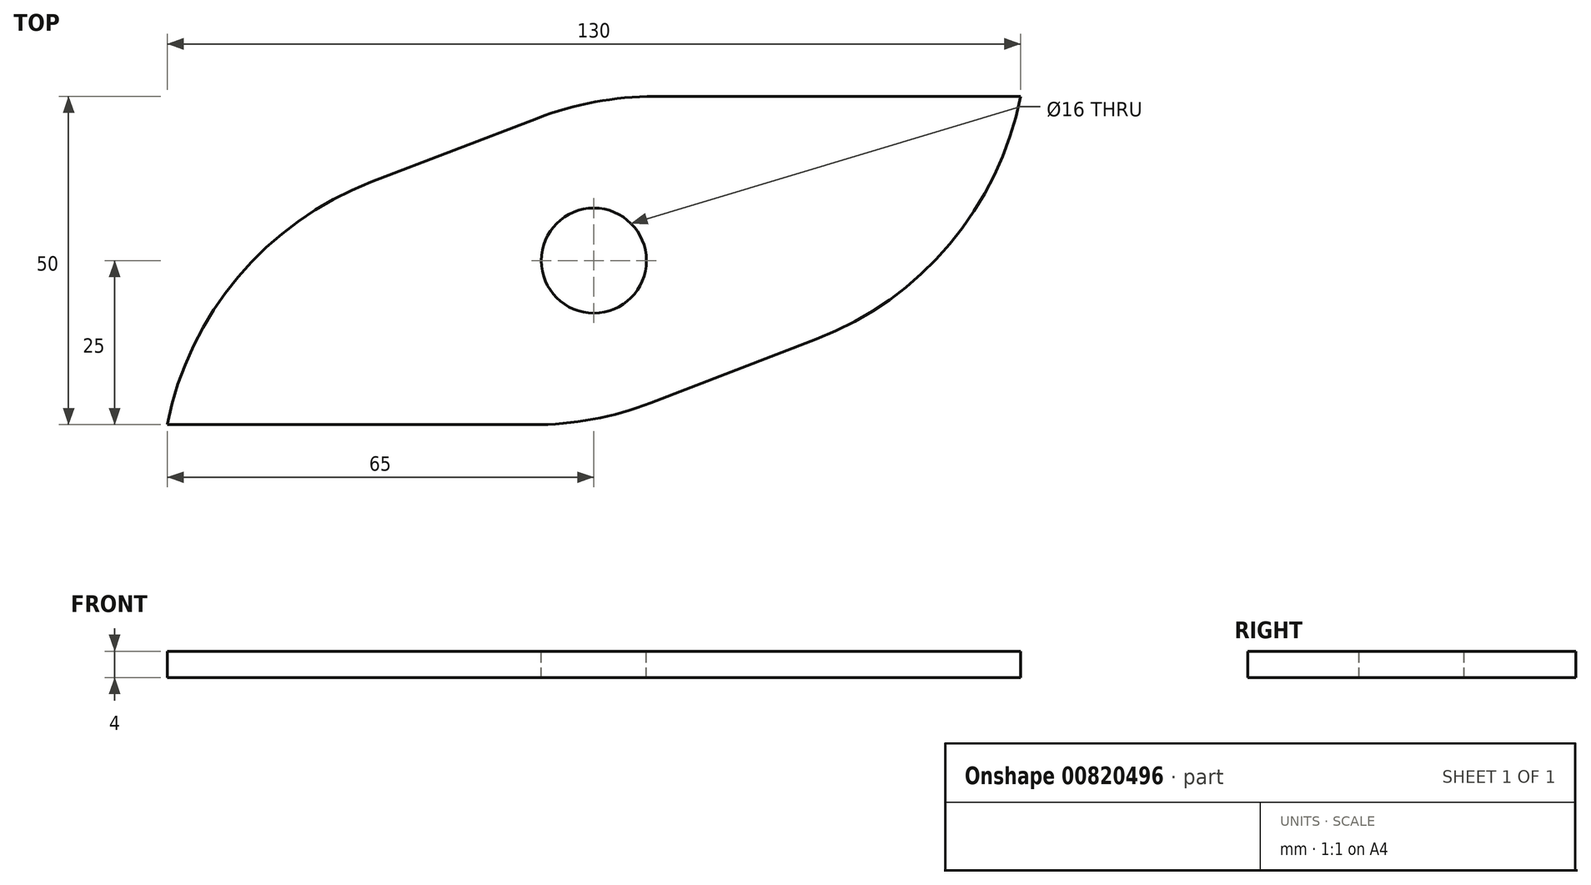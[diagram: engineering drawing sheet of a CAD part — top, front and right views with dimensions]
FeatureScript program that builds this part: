
annotation { "Feature Type Name" : "Feature", "Feature Type Description" : "" }
export const myFeature = defineFeature(function(context is Context, id is Id, definition is map)
    precondition{}
    {
        {
            var Q0;
            Q0=qCreatedBy(makeId("Top.planeOp"),FACE);
            var sketch = newSketch(context, id + "F0", { "sketchPlane" : qUnion([Q0])});
            skLineSegment(sketch, "E0.bottom", {"start": v(65, 25) * mm, "end": v(-65, 25) * mm});
            skLineSegment(sketch, "E0.top", {"start": v(65, -25) * mm, "end": v(-65, -25) * mm});
            skLineSegment(sketch, "E0.left", {"start": v(65, 25) * mm, "end": v(65, -25) * mm});
            skLineSegment(sketch, "E0.right", {"start": v(-65, 25) * mm, "end": v(-65, -25) * mm});
            skPoint(sketch, "E0.middle", {"position": v(0, 0) * mm});
            skLineSegment(sketch, "E1", {"start": v(65, 0) * mm, "end": v(0, -25) * mm});
            skLineSegment(sketch, "E2", {"start": v(-65, 0) * mm, "end": v(0, 25) * mm});
            skSolve(sketch);
        }
        {
            var Q0;
            {var subQ7=sQuery(id+"F0.wireOp",EDGE,"E1");Q0=makeQuery(id+"F0.imprint","IMPRINT",FACE,{"disambiguationData":[TD([[makeQuery(id+"F0.imprint","IMPRINT",EDGE,{"derivedFrom":subQ7}),-1.0]])]});}
            extrude(context, id + "F1", {"entities" : qUnion([Q0]), "depth" : 4 * mm, "offsetDistance" : 25 * mm});
        }
        {
            var Q0;
            Q0=makeQuery(id+"F1.opExtrude","CAP_FACE",FACE,{"disambiguationData":[OSD([sQuery(id+"F0.wireOp",EDGE,"E0.bottom"),sQuery(id+"F0.wireOp",EDGE,"E0.top"),sQuery(id+"F0.wireOp",EDGE,"E0.left"),sQuery(id+"F0.wireOp",EDGE,"E0.right")])],"isStart":false});
            var sketch = newSketch(context, id + "F2", { "sketchPlane" : qUnion([Q0])});
            skCircle(sketch, "E3", {"center": v(0, 0) * mm, "radius": 8 * mm});
            skSolve(sketch);
        }
        {
            var Q0;
            Q0=makeQuery(id+"F2.imprint","IMPRINT",FACE,{"disambiguationData":[TD([[makeQuery(id+"F2.imprint","IMPRINT",EDGE,{"derivedFrom":sQuery(id+"F2.wireOp",EDGE,"E3")}),1.0]])]});
            extrude(context, id + "F3", {"entities" : qUnion([Q0]), "operationType" : NewBodyOperationType.REMOVE, "oppositeDirection" : true, "depth" : 25 * mm, "offsetDistance" : 25 * mm});
        }
        {
            var Q0;
            Q0=makeQuery(id+"F1.opExtrude","SWEPT_EDGE",EDGE,{"disambiguationData":[OSD([sQuery(id+"F0.wireOp",EDGE,"E0.top"),sQuery(id+"F0.wireOp",EDGE,"E1")])]});
            var Q1;
            Q1=makeQuery(id+"F1.opExtrude","SWEPT_EDGE",EDGE,{"disambiguationData":[OSD([sQuery(id+"F0.wireOp",EDGE,"E0.bottom"),sQuery(id+"F0.wireOp",EDGE,"E2")])]});
            var Q2;
            Q2=makeQuery(id+"F1.opExtrude","SWEPT_EDGE",EDGE,{"disambiguationData":[OSD([sQuery(id+"F0.wireOp",EDGE,"E0.right"),sQuery(id+"F0.wireOp",EDGE,"E2")])]});
            var Q3;
            Q3=makeQuery(id+"F1.opExtrude","SWEPT_EDGE",EDGE,{"disambiguationData":[OSD([sQuery(id+"F0.wireOp",EDGE,"E0.left"),sQuery(id+"F0.wireOp",EDGE,"E1")])]});
            fillet(context, id + "F4", {"entities" : qUnion([Q0, Q1, Q2, Q3]), "radius" : 50 * mm, "tangentPropagation" : true, "allowEdgeOverflow" : false});
        }
    });
